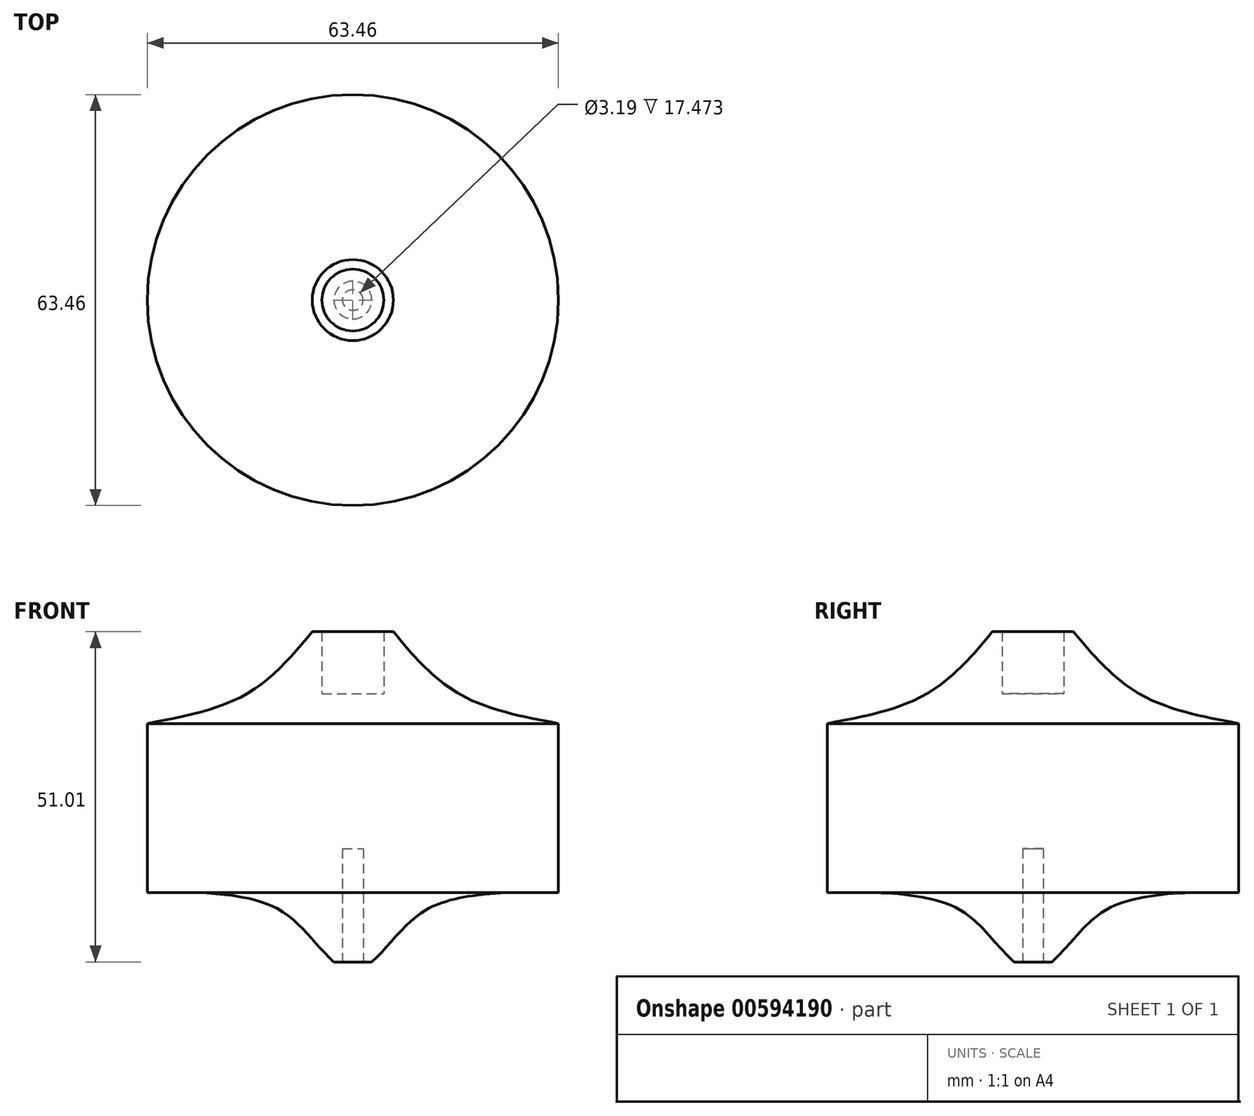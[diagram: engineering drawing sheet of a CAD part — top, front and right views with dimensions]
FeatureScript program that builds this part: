
annotation { "Feature Type Name" : "Feature", "Feature Type Description" : "" }
export const myFeature = defineFeature(function(context is Context, id is Id, definition is map)
    precondition{}
    {
        {
            var Q0;
            Q0=qCreatedBy(makeId("Front.planeOp"),FACE);
            var sketch = newSketch(context, id + "F0", { "sketchPlane" : qUnion([Q0])});
            skLineSegment(sketch, "E0", {"start": v(0, 41.47) * mm, "end": v(4.77, 41.47) * mm});
            skLineSegment(sketch, "E1", {"start": v(4.77, 41.47) * mm, "end": v(4.77, 51.01) * mm});
            skLineSegment(sketch, "E2", {"start": v(1.6, 0) * mm, "end": v(1.6, 17.47) * mm});
            skFitSpline(sketch, "E3", {"points": [v(6.26, 51.01) * mm, v(16.28, 41.47) * mm, v(31.73, 36.83) * mm], "startDerivative": vector(18.7, -22.48) * mm, "endDerivative": vector(32.08, -6.09) * mm});
            skLineSegment(sketch, "E4", {"start": v(4.77, 51.01) * mm, "end": v(6.26, 51.01) * mm});
            skFitSpline(sketch, "E5", {"points": [v(2.92, 0) * mm, v(11.88, 8.35) * mm, v(31.73, 10.72) * mm], "startDerivative": vector(21.16, 18.94) * mm, "endDerivative": vector(36.84, -0.41) * mm});
            skLineSegment(sketch, "E6", {"start": v(1.6, 0) * mm, "end": v(2.92, 0) * mm});
            skLineSegment(sketch, "E7", {"start": v(31.73, 36.83) * mm, "end": v(31.73, 10.72) * mm});
            skLineSegment(sketch, "E8", {"start": v(1.6, 17.47) * mm, "end": v(0, 17.47) * mm});
            skLineSegment(sketch, "E9", {"start": v(0, 17.47) * mm, "end": v(0, 41.47) * mm});
            skSolve(sketch);
        }
        {
            var Q0;
            Q0=makeQuery(id+"F0.imprint","IMPRINT",FACE,{"disambiguationData":[TD([[makeQuery(id+"F0.imprint","IMPRINT",EDGE,{"derivedFrom":sQuery(id+"F0.wireOp",EDGE,"E0")}),-1.0]])]});
            var Q1;
            Q1=sQuery(id+"F0.wireOp",EDGE,"E9");
            revolve(context, id + "F1", {"entities" : qUnion([Q0]), "axis" : qUnion([Q1]), "revolveType" : RevolveType.FULL});
        }
    });
